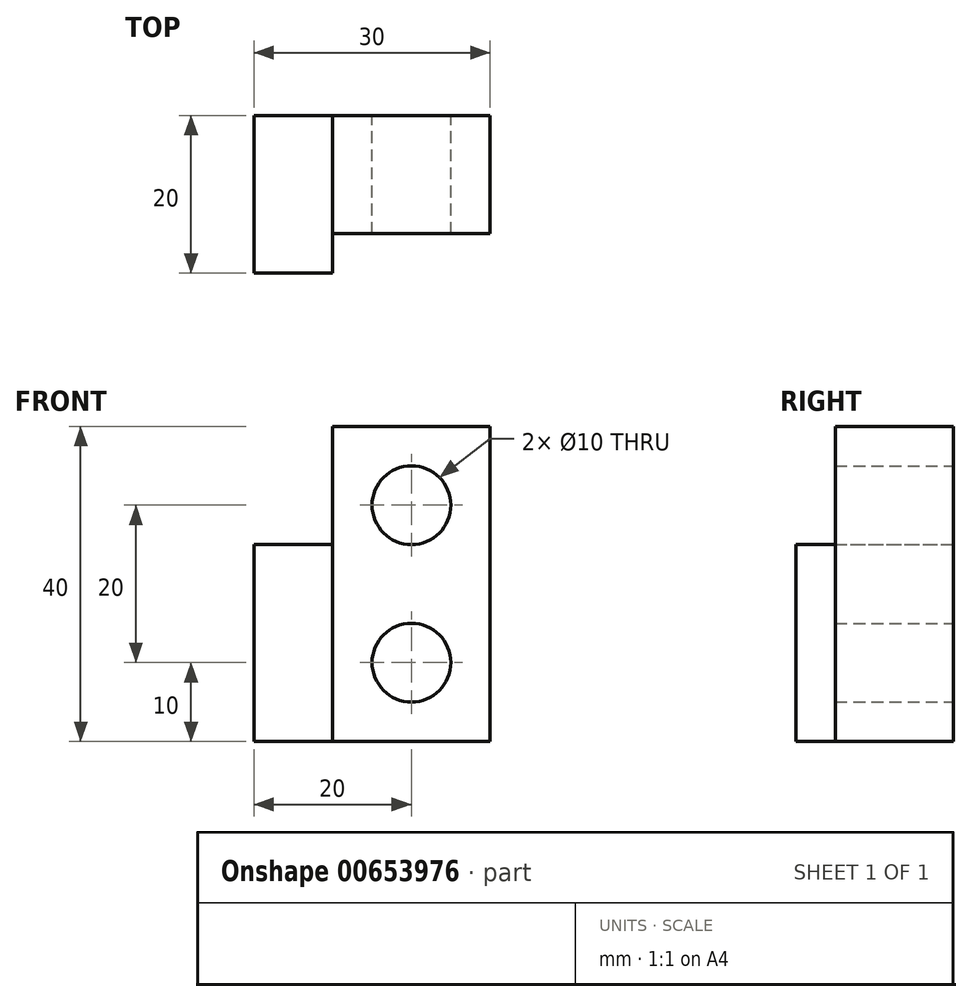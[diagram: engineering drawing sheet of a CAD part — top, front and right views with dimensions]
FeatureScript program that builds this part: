
annotation { "Feature Type Name" : "Feature", "Feature Type Description" : "" }
export const myFeature = defineFeature(function(context is Context, id is Id, definition is map)
    precondition{}
    {
        {
            var Q0;
            Q0=qCreatedBy(makeId("Front.planeOp"),FACE);
            var sketch = newSketch(context, id + "F0", { "sketchPlane" : qUnion([Q0])});
            skLineSegment(sketch, "E0.bottom", {"start": v(-20, 40) * mm, "end": v(0, 40) * mm});
            skLineSegment(sketch, "E0.top", {"start": v(-20, 0) * mm, "end": v(0, 0) * mm});
            skLineSegment(sketch, "E0.left", {"start": v(-20, 40) * mm, "end": v(-20, 0) * mm});
            skLineSegment(sketch, "E0.right", {"start": v(0, 40) * mm, "end": v(0, 0) * mm});
            skLineSegment(sketch, "E1.bottom", {"start": v(-30, 25) * mm, "end": v(-20, 25) * mm});
            skLineSegment(sketch, "E1.top", {"start": v(-30, 0) * mm, "end": v(-20, 0) * mm});
            skLineSegment(sketch, "E1.left", {"start": v(-30, 25) * mm, "end": v(-30, 0) * mm});
            skLineSegment(sketch, "E1.right", {"start": v(-20, 25) * mm, "end": v(-20, 0) * mm});
            skCircle(sketch, "E2", {"center": v(-10, 30) * mm, "radius": 5 * mm});
            skCircle(sketch, "E3", {"center": v(-10, 10) * mm, "radius": 5 * mm});
            skSolve(sketch);
        }
        {
            var Q0;
            Q0=makeQuery(id+"F0.imprint","IMPRINT",FACE,{"disambiguationData":[TD([[makeQuery(id+"F0.imprint","IMPRINT",EDGE,{"derivedFrom":sQuery(id+"F0.wireOp",EDGE,"E1.bottom")}),-1.0]])]});
            extrude(context, id + "F1", {"entities" : qUnion([Q0]), "depth" : 20 * mm, "offsetDistance" : 25 * mm});
        }
        {
            var Q0;
            Q0=makeQuery(id+"F0.imprint","IMPRINT",FACE,{"disambiguationData":[TD([[makeQuery(id+"F0.imprint","IMPRINT",EDGE,{"derivedFrom":sQuery(id+"F0.wireOp",EDGE,"E0.bottom")}),-1.0]])]});
            extrude(context, id + "F2", {"entities" : qUnion([Q0]), "operationType" : NewBodyOperationType.ADD, "depth" : 15 * mm, "offsetDistance" : 25 * mm});
        }
    });
